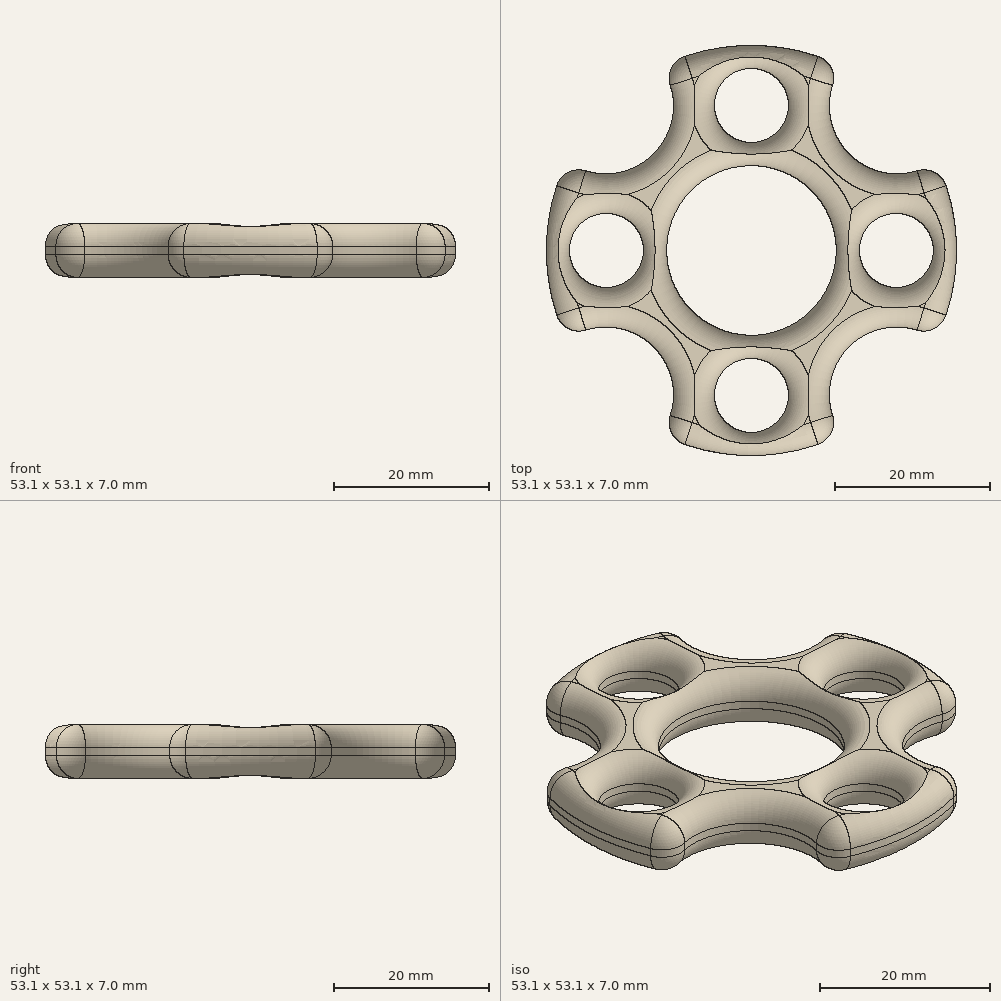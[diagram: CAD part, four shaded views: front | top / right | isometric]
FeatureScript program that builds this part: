
annotation { "Feature Type Name" : "Feature", "Feature Type Description" : "" }
export const myFeature = defineFeature(function(context is Context, id is Id, definition is map)
    precondition{}
    {
        {
            var Q0;
            Q0=qCreatedBy(makeId("Top.planeOp"),FACE);
            var sketch = newSketch(context, id + "F0", { "sketchPlane" : qUnion([Q0])});
            skCircle(sketch, "E0", {"center": v(0, 0) * mm, "radius": 10.98 * mm});
            skArc(sketch, "E1", {"start": v(11.74, 23.82) * mm, "mid": v(0, 26.56) * mm, "end": v(-11.74, 23.82) * mm});
            skCircle(sketch, "E2", {"center": v(0, -18.77) * mm, "radius": 4.79 * mm});
            skCircle(sketch, "E3", {"center": v(-18.77, 0) * mm, "radius": 4.79 * mm});
            skCircle(sketch, "E4", {"center": v(18.77, 0) * mm, "radius": 4.79 * mm});
            skCircle(sketch, "E5", {"center": v(0, 18.77) * mm, "radius": 4.79 * mm});
            skArc(sketch, "E6", {"start": v(23.92, -11.52) * mm, "mid": v(12.63, -12.52) * mm, "end": v(11.74, -23.82) * mm});
            skArc(sketch, "E7", {"start": v(-11.74, -23.82) * mm, "mid": v(-12.63, -12.52) * mm, "end": v(-23.92, -11.52) * mm});
            skArc(sketch, "E8", {"start": v(-23.92, 11.52) * mm, "mid": v(-12.63, 12.52) * mm, "end": v(-11.74, 23.82) * mm});
            skArc(sketch, "E9", {"start": v(11.74, 23.82) * mm, "mid": v(12.63, 12.52) * mm, "end": v(23.92, 11.52) * mm});
            skArc(sketch, "E10.trimOffspring", {"start": v(-23.92, 11.52) * mm, "mid": v(-26.55, 0) * mm, "end": v(-23.92, -11.52) * mm});
            skArc(sketch, "E11.trimOffspring", {"start": v(-11.74, -23.82) * mm, "mid": v(0, -26.56) * mm, "end": v(11.74, -23.82) * mm});
            skArc(sketch, "E12.trimOffspring", {"start": v(23.92, -11.52) * mm, "mid": v(26.55, 0) * mm, "end": v(23.92, 11.52) * mm});
            skSolve(sketch);
        }
        {
            var Q0;
            Q0=makeQuery(id+"F0.imprint","IMPRINT",FACE,{"disambiguationData":[TD([[makeQuery(id+"F0.imprint","IMPRINT",EDGE,{"derivedFrom":sQuery(id+"F0.wireOp",EDGE,"E0")}),-1.0]])]});
            extrude(context, id + "F1", {"entities" : qUnion([Q0]), "depth" : 7 * mm, "offsetDistance" : 25 * mm});
        }
        {
            var Q0;
            Q0=makeQuery(id+"F1.opExtrude","CAP_FACE",FACE,{"disambiguationData":[OSD([sQuery(id+"F0.wireOp",EDGE,"E0"),sQuery(id+"F0.wireOp",EDGE,"E1"),sQuery(id+"F0.wireOp",EDGE,"E2"),sQuery(id+"F0.wireOp",EDGE,"E3"),sQuery(id+"F0.wireOp",EDGE,"E4"),sQuery(id+"F0.wireOp",EDGE,"E5"),sQuery(id+"F0.wireOp",EDGE,"E6"),sQuery(id+"F0.wireOp",EDGE,"E7"),sQuery(id+"F0.wireOp",EDGE,"E8"),sQuery(id+"F0.wireOp",EDGE,"E9")])],"isStart":false});
            var Q1;
            Q1=makeQuery(id+"F1.opExtrude","CAP_FACE",FACE,{"disambiguationData":[OSD([sQuery(id+"F0.wireOp",EDGE,"E0"),sQuery(id+"F0.wireOp",EDGE,"E1"),sQuery(id+"F0.wireOp",EDGE,"E2"),sQuery(id+"F0.wireOp",EDGE,"E3"),sQuery(id+"F0.wireOp",EDGE,"E4"),sQuery(id+"F0.wireOp",EDGE,"E5"),sQuery(id+"F0.wireOp",EDGE,"E6"),sQuery(id+"F0.wireOp",EDGE,"E7"),sQuery(id+"F0.wireOp",EDGE,"E8"),sQuery(id+"F0.wireOp",EDGE,"E9")])],"isStart":true});
            var Q2;
            Q2=makeQuery(id+"F1.opExtrude","SWEPT_EDGE",EDGE,{"disambiguationData":[OSD([sQuery(id+"F0.wireOp",EDGE,"E1"),sQuery(id+"F0.wireOp",EDGE,"E8")])]});
            var Q3;
            Q3=makeQuery(id+"F1.opExtrude","SWEPT_EDGE",EDGE,{"disambiguationData":[OSD([sQuery(id+"F0.wireOp",EDGE,"E8"),sQuery(id+"F0.wireOp",EDGE,"E10.trimOffspring")])]});
            var Q4;
            Q4=makeQuery(id+"F1.opExtrude","SWEPT_EDGE",EDGE,{"disambiguationData":[OSD([sQuery(id+"F0.wireOp",EDGE,"E7"),sQuery(id+"F0.wireOp",EDGE,"E10.trimOffspring")])]});
            var Q5;
            Q5=makeQuery(id+"F1.opExtrude","SWEPT_EDGE",EDGE,{"disambiguationData":[OSD([sQuery(id+"F0.wireOp",EDGE,"E7"),sQuery(id+"F0.wireOp",EDGE,"E11.trimOffspring")])]});
            var Q6;
            Q6=makeQuery(id+"F1.opExtrude","SWEPT_EDGE",EDGE,{"disambiguationData":[OSD([sQuery(id+"F0.wireOp",EDGE,"E6"),sQuery(id+"F0.wireOp",EDGE,"E11.trimOffspring")])]});
            var Q7;
            Q7=makeQuery(id+"F1.opExtrude","SWEPT_EDGE",EDGE,{"disambiguationData":[OSD([sQuery(id+"F0.wireOp",EDGE,"E6"),sQuery(id+"F0.wireOp",EDGE,"E12.trimOffspring")])]});
            var Q8;
            Q8=makeQuery(id+"F1.opExtrude","SWEPT_EDGE",EDGE,{"disambiguationData":[OSD([sQuery(id+"F0.wireOp",EDGE,"E9"),sQuery(id+"F0.wireOp",EDGE,"E12.trimOffspring")])]});
            var Q9;
            Q9=makeQuery(id+"F1.opExtrude","SWEPT_EDGE",EDGE,{"disambiguationData":[OSD([sQuery(id+"F0.wireOp",EDGE,"E1"),sQuery(id+"F0.wireOp",EDGE,"E9")])]});
            fillet(context, id + "F2", {"entities" : qUnion([Q0, Q1, Q2, Q3, Q4, Q5, Q6, Q7, Q8, Q9]), "radius" : 3 * mm, "tangentPropagation" : true, "allowEdgeOverflow" : false});
        }
    });
